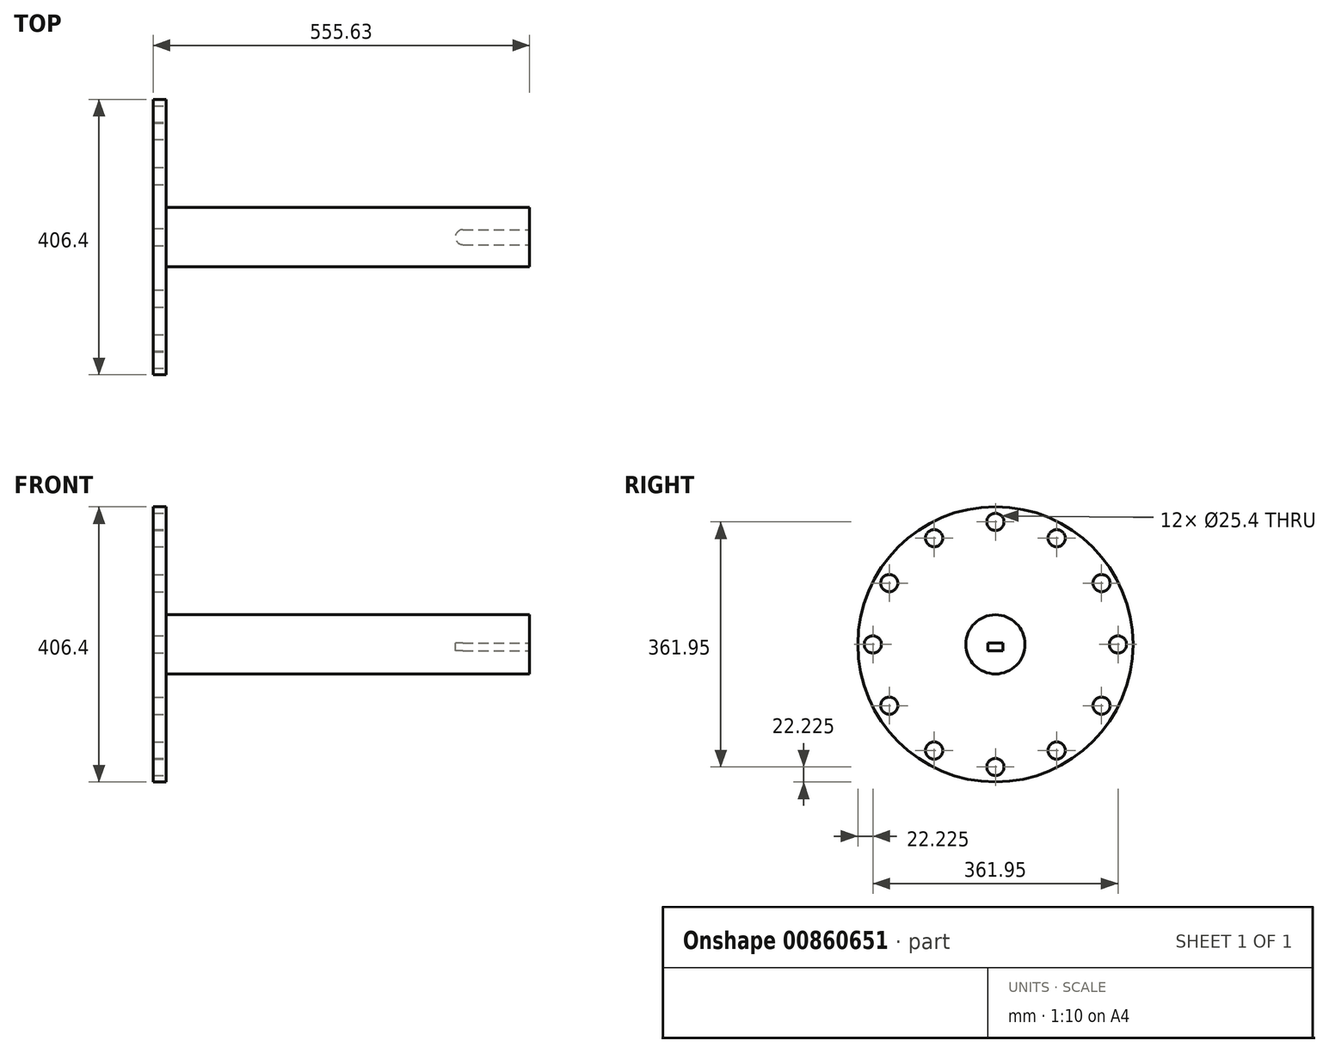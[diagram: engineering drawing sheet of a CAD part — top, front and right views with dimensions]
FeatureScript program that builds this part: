
annotation { "Feature Type Name" : "Feature", "Feature Type Description" : "" }
export const myFeature = defineFeature(function(context is Context, id is Id, definition is map)
    precondition{}
    {
        {
            var Q0;
            Q0=qCreatedBy(makeId("Front.planeOp"),FACE);
            var sketch = newSketch(context, id + "F0", { "sketchPlane" : qUnion([Q0])});
            skLineSegment(sketch, "E0", {"start": v(0, 0) * mm, "end": v(0, 203.2) * mm});
            skLineSegment(sketch, "E1", {"start": v(0, 203.2) * mm, "end": v(19.05, 203.2) * mm});
            skLineSegment(sketch, "E2", {"start": v(19.05, 203.2) * mm, "end": v(19.05, 43.66) * mm});
            skLineSegment(sketch, "E3", {"start": v(19.05, 43.66) * mm, "end": v(555.62, 43.66) * mm});
            skLineSegment(sketch, "E4", {"start": v(555.62, 43.66) * mm, "end": v(555.62, 0) * mm});
            skLineSegment(sketch, "E5", {"start": v(555.62, 0) * mm, "end": v(0, 0) * mm});
            skSolve(sketch);
        }
        {
            var Q0;
            Q0=makeQuery(id+"F0.imprint","IMPRINT",FACE,{"disambiguationData":[TD([[makeQuery(id+"F0.imprint","IMPRINT",EDGE,{"derivedFrom":sQuery(id+"F0.wireOp",EDGE,"E0")}),-1.0]])]});
            var Q1;
            Q1=sQuery(id+"F0.wireOp",EDGE,"E5");
            revolve(context, id + "F1", {"surfaceOperationType" : NewSurfaceOperationType.NEW, "entities" : qUnion([Q0]), "axis" : qUnion([Q1]), "revolveType" : RevolveType.FULL});
        }
        {
            var Q0;
            Q0=makeQuery(id+"F1.opRevolve","SWEPT_FACE",FACE,{"disambiguationData":[OSD([sQuery(id+"F0.wireOp",EDGE,"E2")])]});
            var sketch = newSketch(context, id + "F2", { "sketchPlane" : qUnion([Q0])});
            skLineSegment(sketch, "E6", {"start": v(0, 0) * mm, "end": v(0, 180.98) * mm, "construction": true});
            skPoint(sketch, "E7", {"position": v(0, 180.98) * mm});
            skPoint(sketch, "E8.1.0", {"position": v(-90.49, 156.73) * mm});
            skPoint(sketch, "E8.2.0", {"position": v(-156.73, 90.49) * mm});
            skPoint(sketch, "E8.3.0", {"position": v(-180.98, 0) * mm});
            skPoint(sketch, "E8.4.0", {"position": v(-156.73, -90.49) * mm});
            skPoint(sketch, "E8.5.0", {"position": v(-90.49, -156.73) * mm});
            skPoint(sketch, "E8.6.0", {"position": v(0, -180.98) * mm});
            skPoint(sketch, "E8.7.0", {"position": v(90.49, -156.73) * mm});
            skPoint(sketch, "E8.8.0", {"position": v(156.73, -90.49) * mm});
            skPoint(sketch, "E8.9.0", {"position": v(180.98, 0) * mm});
            skPoint(sketch, "E8.10.0", {"position": v(156.73, 90.49) * mm});
            skPoint(sketch, "E8.11.0", {"position": v(90.49, 156.73) * mm});
            skPoint(sketch, "E8.center", {"position": v(0, 0) * mm});
            skSolve(sketch);
        }
        {
            var Q0;
            Q0=sQuery(id+"F2.wireOp",VERTEX,"E7");
            var Q1;
            Q1=sQuery(id+"F2.wireOp",VERTEX,"E8.11.0");
            var Q2;
            Q2=sQuery(id+"F2.wireOp",VERTEX,"E8.10.0");
            var Q3;
            Q3=sQuery(id+"F2.wireOp",VERTEX,"E8.9.0");
            var Q4;
            Q4=sQuery(id+"F2.wireOp",VERTEX,"E8.8.0");
            var Q5;
            Q5=sQuery(id+"F2.wireOp",VERTEX,"E8.7.0");
            var Q6;
            Q6=sQuery(id+"F2.wireOp",VERTEX,"E8.6.0");
            var Q7;
            Q7=sQuery(id+"F2.wireOp",VERTEX,"E8.5.0");
            var Q8;
            Q8=sQuery(id+"F2.wireOp",VERTEX,"E8.4.0");
            var Q9;
            Q9=sQuery(id+"F2.wireOp",VERTEX,"E8.3.0");
            var Q10;
            Q10=sQuery(id+"F2.wireOp",VERTEX,"E8.2.0");
            var Q11;
            Q11=sQuery(id+"F2.wireOp",VERTEX,"E8.1.0");
            var Q12;
            Q12=makeQuery(id+"F1.opRevolve","SWEPT_BODY",BODY,{"disambiguationData":[OSD([sQuery(id+"F0.wireOp",EDGE,"E0"),sQuery(id+"F0.wireOp",EDGE,"E1"),sQuery(id+"F0.wireOp",EDGE,"E2"),sQuery(id+"F0.wireOp",EDGE,"E3"),sQuery(id+"F0.wireOp",EDGE,"E4"),sQuery(id+"F0.wireOp",EDGE,"E5")])]});
            hole(context, id + "F3", {"style" : HoleStyle.SIMPLE, "endStyle" : HoleEndStyle.THROUGH, "holeDiameter" : 25.4 * mm, "majorDiameter" : 6.35 * mm, "isTappedThrough" : true, "tappedDepth" : 12.7 * mm, "tapClearance" : 3, "locations" : qUnion([Q0, Q1, Q2, Q3, Q4, Q5, Q6, Q7, Q8, Q9, Q10, Q11]), "scope" : qUnion([Q12])});
        }
        {
            var Q0;
            Q0=qCreatedBy(makeId("Top.planeOp"),FACE);
            cPlane(context, id + "F4", {"entities" : qUnion([Q0]), "cplaneType" : CPlaneType.OFFSET, "offset" : (((7 / 16) + 3) / 2) * mm, "width" : 152.4 * mm, "height" : 152.4 * mm});
        }
        {
            var Q0;
            Q0=qCreatedBy(id+"F4.planeOp",FACE);
            var sketch = newSketch(context, id + "F5", { "sketchPlane" : qUnion([Q0])});
            skLineSegment(sketch, "E9.0", {"start": v(555.62, 43.66) * mm, "end": v(555.62, -43.66) * mm});
            skLineSegment(sketch, "E10", {"start": v(555.62, 0) * mm, "end": v(457.2, 0) * mm, "construction": true});
            skArc(sketch, "E11", {"start": v(457.2, 11.11) * mm, "mid": v(446.09, 0) * mm, "end": v(457.2, -11.11) * mm});
            skLineSegment(sketch, "E12", {"start": v(457.2, 11.11) * mm, "end": v(555.62, 11.11) * mm});
            skLineSegment(sketch, "E13", {"start": v(457.2, -11.11) * mm, "end": v(555.62, -11.11) * mm});
            skSolve(sketch);
        }
        {
            var Q0;
            Q0=makeQuery(id+"F5.imprint","IMPRINT",FACE,{"disambiguationData":[TD([[makeQuery(id+"F5.imprint","IMPRINT",EDGE,{"derivedFrom":sQuery(id+"F5.wireOp",EDGE,"E11")}),1.0]])]});
            extrude(context, id + "F6", {"entities" : qUnion([Q0]), "operationType" : NewBodyOperationType.REMOVE, "oppositeDirection" : true, "depth" : 11.1 * mm, "offsetDistance" : 25.4 * mm});
        }
    });
